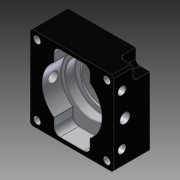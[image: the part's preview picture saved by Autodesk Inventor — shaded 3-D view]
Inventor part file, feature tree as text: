
AUTODESK INVENTOR PART (.ipt)
format: ipt  version: 2014 SP1 (Build 180222100, 222)  size: 325,632 bytes
history: native  units: in
note: dims shown in document units (in); Inventor stores cm internally (conversion verified against a paired STEP export)
features: hole x1, other x1, imported_body x1
ambient origin geometry x8: Origin, YZ Plane, XZ Plane, XY Plane, X Axis, Y Axis, Z Axis, Center Point
bodies: Body1 (feature_tree)
feature tree (3):
  hole  "Hole1"  [1 undecoded]
  other  "217-2625-001 Rev1.ipt1"
  imported_body  "Base1"
note: 1 required parameter value undecoded (feature->parameter linkage not recoverable at this tier; creation-order binding heuristic only, values carry confidence <= 0.55)
